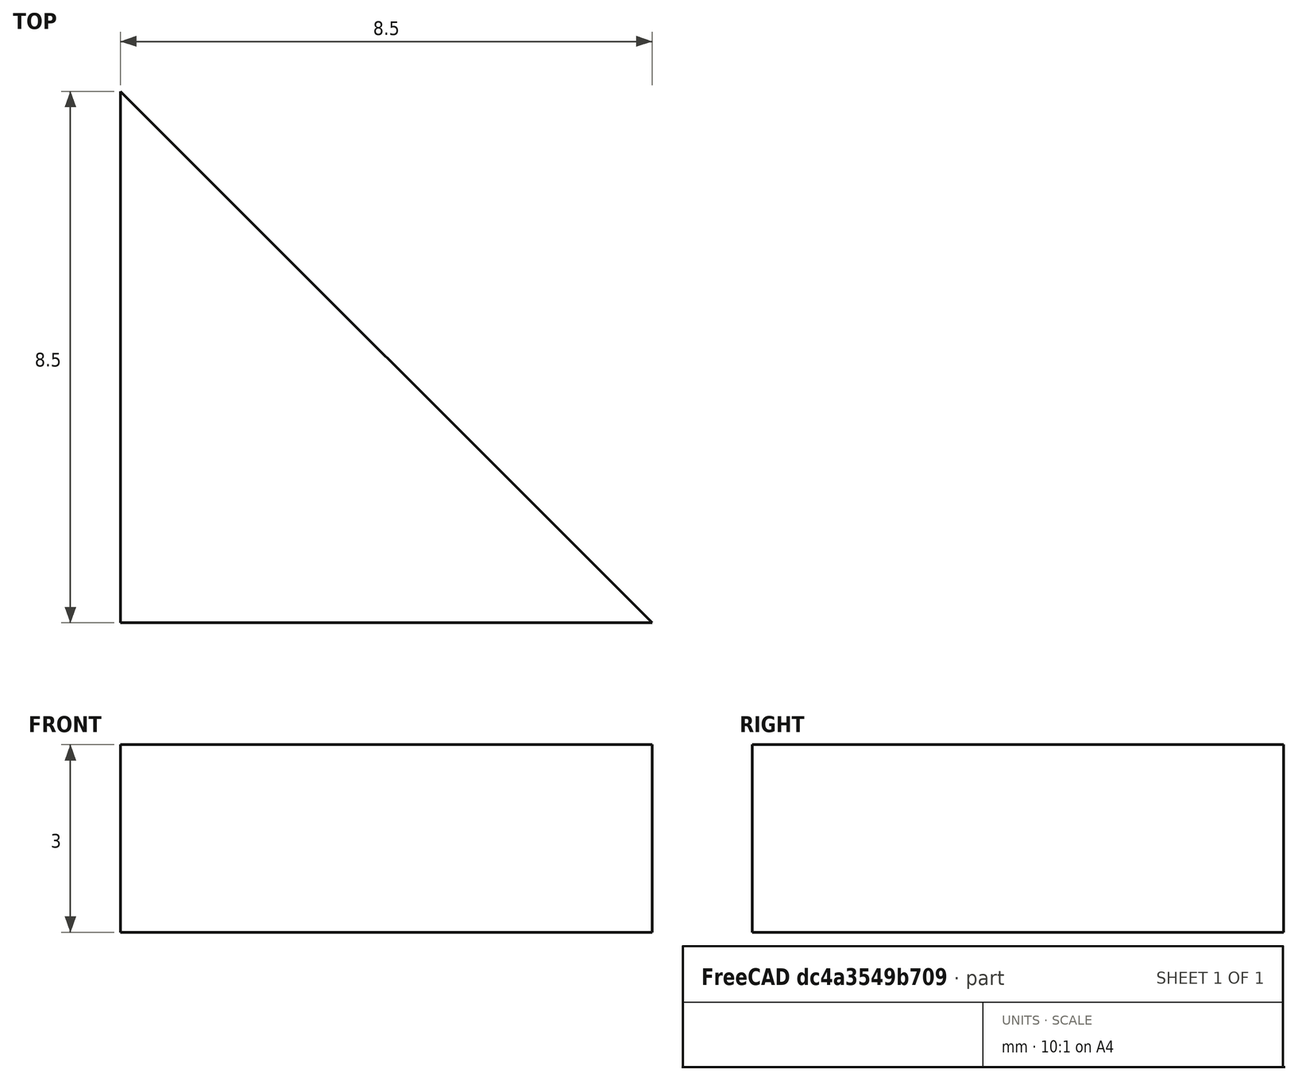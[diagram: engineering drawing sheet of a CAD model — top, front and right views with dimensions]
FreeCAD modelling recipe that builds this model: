
FCSTD DOCUMENT  (FreeCAD 0.21R33694 (Git))
Label: kumiko_box_key_miter
License: All rights reserved
LicenseURL: https://en.wikipedia.org/wiki/All_rights_reserved
objects: Sketcher::SketchObject×1, PartDesign::Pad×1, PartDesign::Body×1, App::Link×1
note: 4 computed .brp shape members not serialized (recipe doc carries the construction recipe); baked Part::Feature solids carry a one-line shape summary decoded from their .brp
EXTERNAL_REF file=../../master_kumiko_box.FCStd obj=Spreadsheet

FEATURE [Sketcher::SketchObject] Sketch027  label="miter_key_drawing"
  FullyConstrained = true
  MapMode = 5
  Support = -> [XY_Plane016]
  expr: Constraints[6] = <<SpreadSheet>>.lid_frame_width
  expr: Constraints[7] = 0
  expr: Constraints[8] = 0
  sketch-geometry (3):
    g0: LineSegment StartX=0 StartY=8.5 StartZ=0 EndX=0 EndY=0 EndZ=0
    g1: LineSegment StartX=0 StartY=0 StartZ=0 EndX=8.5 EndY=0 EndZ=0
    g2: LineSegment StartX=8.5 StartY=0 StartZ=0 EndX=0 EndY=8.5 EndZ=0
  constraints (9):
    c: Vertical(g0)
    c: Coincident(g1,g0)
    c: Horizontal(g1)
    c: Coincident(g2,g1)
    c: Coincident(g2,g0)
    c: Equal(g0,g1)
    c: DistanceX(g1,g1) = 8.5
    c: DistanceX(g-1,g0) = 0
    c: DistanceY(g0,g-1) = 0
FEATURE [PartDesign::Pad] Pad012  label="miter_key_extrude"
  Direction = (0,0,1)
  Length = 3
  Length2 = 10
  Profile = -> Sketch027
  ReferenceAxis = -> Sketch027 [N_Axis]
  Type = 0
  expr: Length = <<SpreadSheet>>.kumiko_thickness
FEATURE [PartDesign::Body] Body014  label="miter_key"
  Group = -> [Sketch027,Pad012]
  Origin = -> Origin016
  Tip = -> Pad012
  expr: .Placement.Base.x = 0
  expr: .Placement.Base.y = 0
  expr: .Placement.Base.z = 0
  expr: .Placement.Rotation.Angle = 0
  expr: .Placement.Rotation.Axis.x = 0
  expr: .Placement.Rotation.Axis.y = 0
  expr: .Placement.Rotation.Axis.z = 1
FEATURE [App::Link] Link  label="SpreadSheet"
  LinkedObject = -> <external ../../master_kumiko_box.FCStd>#Spreadsheet
